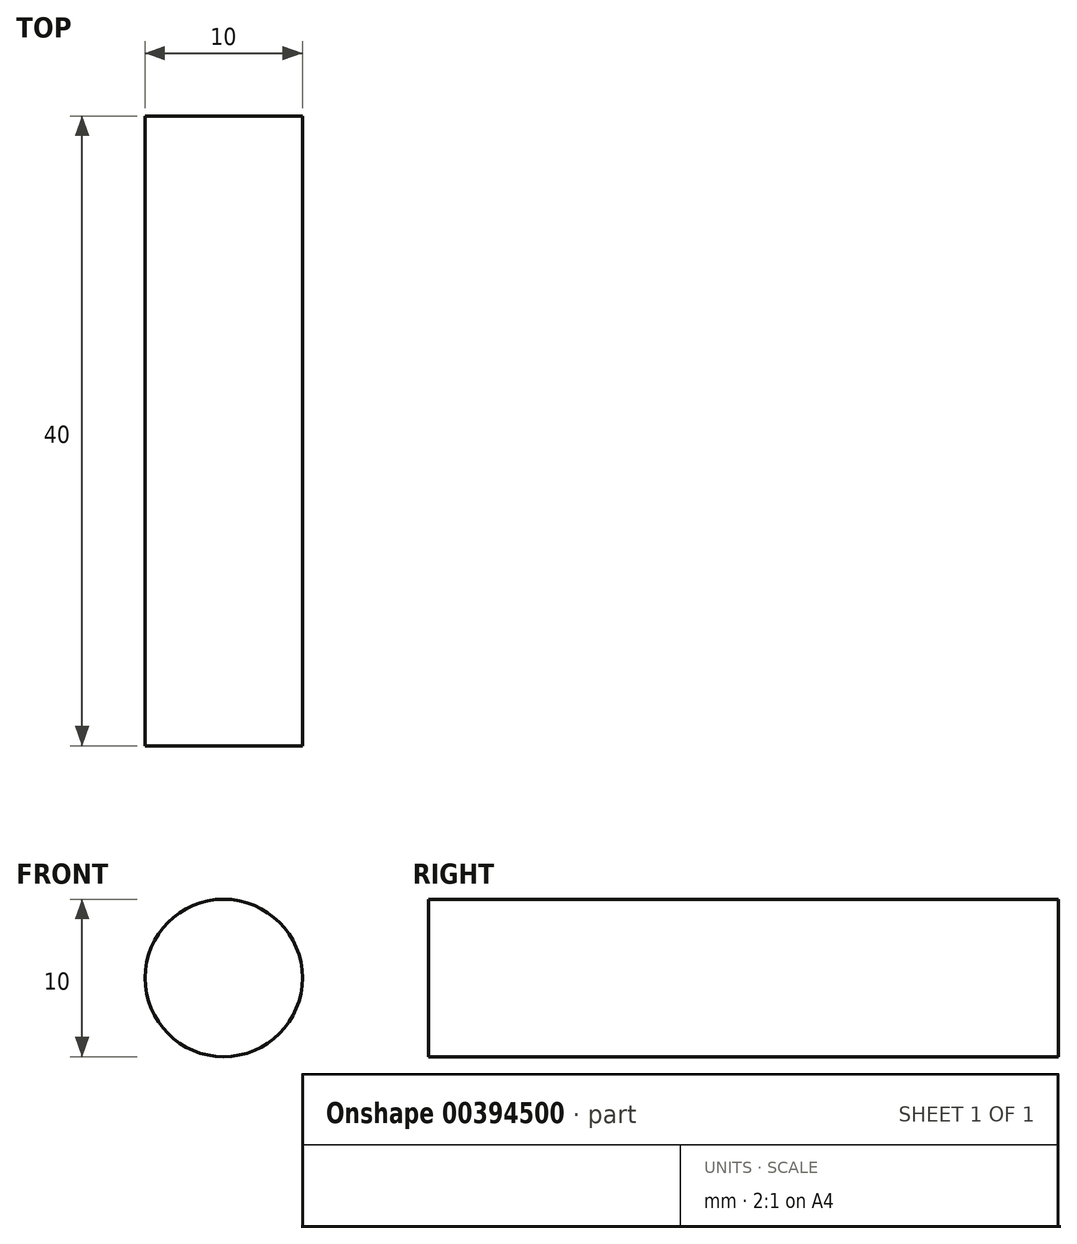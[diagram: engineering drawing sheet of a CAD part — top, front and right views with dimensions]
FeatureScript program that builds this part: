
annotation { "Feature Type Name" : "Feature", "Feature Type Description" : "" }
export const myFeature = defineFeature(function(context is Context, id is Id, definition is map)
    precondition{}
    {
        {
            var Q0;
            Q0=qCreatedBy(makeId("Front.planeOp"),FACE);
            var sketch = newSketch(context, id + "F0", { "sketchPlane" : qUnion([Q0])});
            skCircle(sketch, "E0", {"center": v(0, 0) * mm, "radius": 5 * mm});
            skSolve(sketch);
        }
        {
            var Q0;
            Q0=makeQuery(id+"F0.imprint","IMPRINT",FACE,{"disambiguationData":[TD([[makeQuery(id+"F0.imprint","IMPRINT",EDGE,{"derivedFrom":sQuery(id+"F0.wireOp",EDGE,"E0")}),1.0]])]});
            extrude(context, id + "F1", {"entities" : qUnion([Q0]), "depth" : 40 * mm, "offsetDistance" : 25 * mm, "symmetric" : true});
        }
    });
